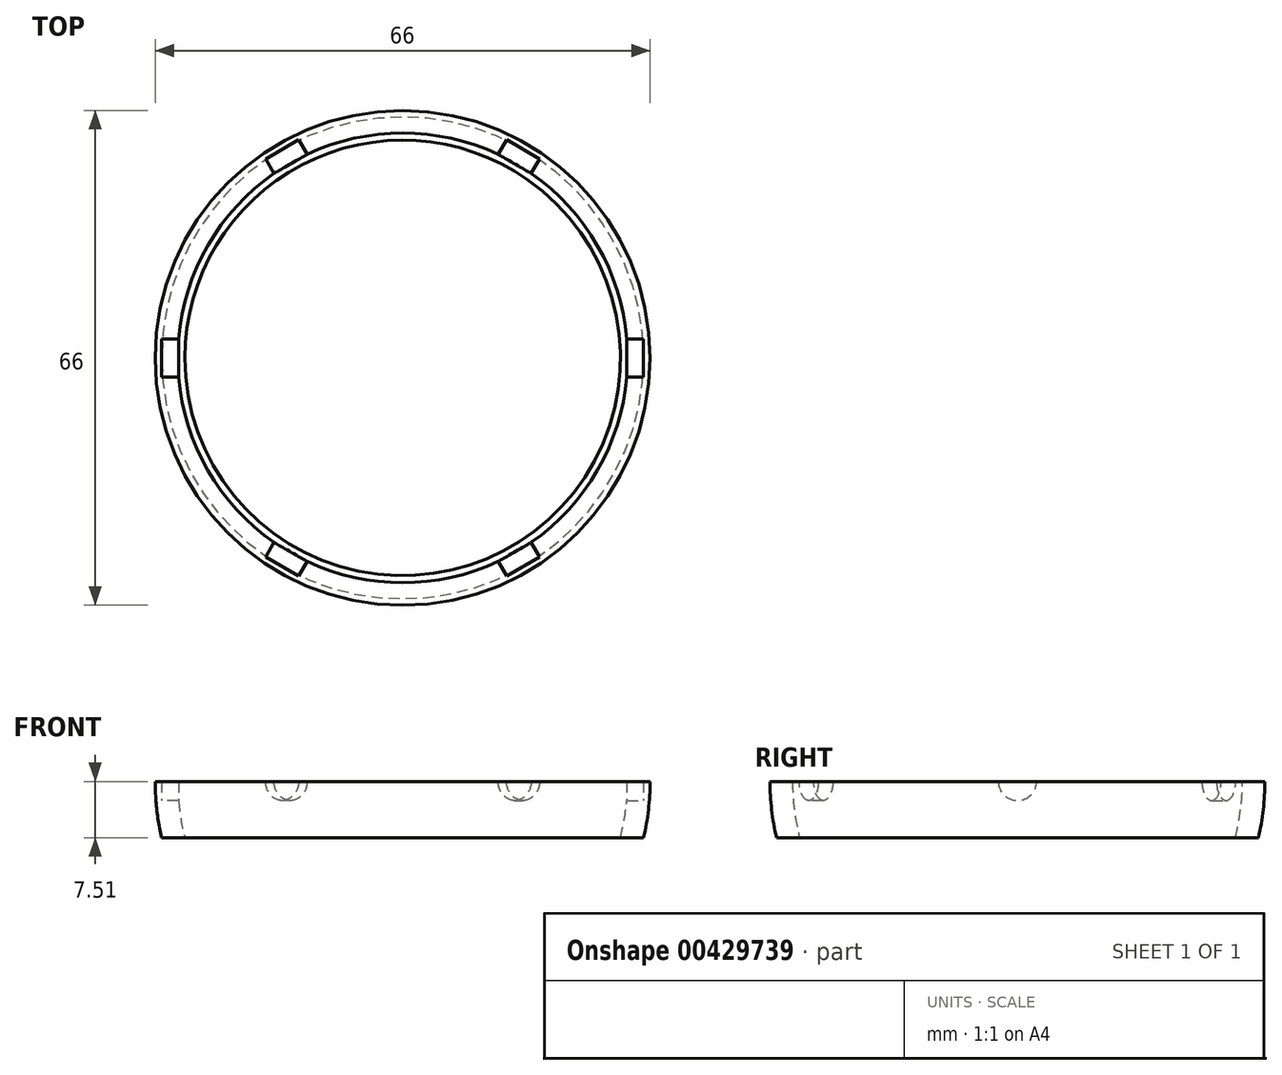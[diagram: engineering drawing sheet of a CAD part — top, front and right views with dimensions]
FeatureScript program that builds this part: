
annotation { "Feature Type Name" : "Feature", "Feature Type Description" : "" }
export const myFeature = defineFeature(function(context is Context, id is Id, definition is map)
    precondition{}
    {
        {
            var Q0;
            Q0=qCreatedBy(makeId("Front.planeOp"),FACE);
            var sketch = newSketch(context, id + "F0", { "sketchPlane" : qUnion([Q0])});
            skLineSegment(sketch, "E0", {"start": v(0, 0) * mm, "end": v(0, 51.6) * mm, "construction": true});
            skArc(sketch, "E1", {"start": v(0, 30) * mm, "mid": v(21.21, 21.21) * mm, "end": v(30, 0) * mm});
            skArc(sketch, "E2", {"start": v(0, 33) * mm, "mid": v(23.33, 23.33) * mm, "end": v(33, 0) * mm});
            skLineSegment(sketch, "E3", {"start": v(30, 0) * mm, "end": v(33, 0) * mm});
            skLineSegment(sketch, "E4", {"start": v(0, 33) * mm, "end": v(0, 30) * mm});
            skLineSegment(sketch, "E5", {"start": v(0, 0) * mm, "end": v(31, 11.29) * mm, "construction": true});
            skLineSegment(sketch, "E6", {"start": v(0, 0) * mm, "end": v(25.28, 21.21) * mm, "construction": true});
            skLineSegment(sketch, "E7", {"start": v(0, 0) * mm, "end": v(16.5, 28.58) * mm, "construction": true});
            skLineSegment(sketch, "E8", {"start": v(5.73, 32.5) * mm, "end": v(0, 0) * mm, "construction": true});
            skLineSegment(sketch, "E9", {"start": v(31, 11.29) * mm, "end": v(35.12, 0) * mm, "construction": true});
            skLineSegment(sketch, "E10", {"start": v(25.28, 21.21) * mm, "end": v(43.08, 0) * mm, "construction": true});
            skLineSegment(sketch, "E11", {"start": v(16.5, 28.58) * mm, "end": v(31, 20.2) * mm, "construction": true});
            skLineSegment(sketch, "E12", {"start": v(5.73, 32.5) * mm, "end": v(16.5, 30.6) * mm, "construction": true});
            skArc(sketch, "E13", {"start": v(30, 0) * mm, "mid": v(29.76, -3.79) * mm, "end": v(29.04, -7.51) * mm});
            skArc(sketch, "E14", {"start": v(33, 0) * mm, "mid": v(32.78, -3.78) * mm, "end": v(32.13, -7.51) * mm});
            skLineSegment(sketch, "E15", {"start": v(32.13, -7.51) * mm, "end": v(29.04, -7.51) * mm});
            skSolve(sketch);
        }
        {
            var Q0;
            Q0=makeQuery(id+"F0.imprint","IMPRINT",FACE,{"disambiguationData":[TD([[makeQuery(id+"F0.imprint","IMPRINT",EDGE,{"derivedFrom":sQuery(id+"F0.wireOp",EDGE,"E1")}),1.0]])]});
            var Q1;
            Q1=makeQuery(id+"F0.imprint","IMPRINT",FACE,{"disambiguationData":[TD([[makeQuery(id+"F0.imprint","IMPRINT",EDGE,{"derivedFrom":sQuery(id+"F0.wireOp",EDGE,"E3")}),-1.0]])]});
            var Q2;
            Q2=sQuery(id+"F0.wireOp",EDGE,"E0");
            revolve(context, id + "F1", {"entities" : qUnion([Q0, Q1]), "axis" : qUnion([Q2]), "revolveType" : RevolveType.SYMMETRIC, "angle" : 60 * degree});
        }
        {
            var Q0;
            Q0=sQuery(id+"F0.wireOp",EDGE,"E9");
            cPlane(context, id + "F2", {"entities" : qUnion([Q0]), "cplaneType" : CPlaneType.LINE_ANGLE, "offset" : 25 * mm, "angle" : 0 * degree, "width" : 150 * mm, "height" : 150 * mm});
        }
        {
            var Q0;
            Q0=sQuery(id+"F0.wireOp",EDGE,"E10");
            cPlane(context, id + "F3", {"entities" : qUnion([Q0]), "cplaneType" : CPlaneType.LINE_ANGLE, "offset" : 25 * mm, "angle" : 0 * degree, "width" : 150 * mm, "height" : 150 * mm});
        }
        {
            var Q0;
            Q0=sQuery(id+"F0.wireOp",EDGE,"E11");
            var Q1;
            Q1=qCreatedBy(makeId("Top.planeOp"),FACE);
            cPlane(context, id + "F4", {"entities" : qUnion([Q0, Q1]), "cplaneType" : CPlaneType.LINE_ANGLE, "offset" : 25 * mm, "angle" : 0 * degree, "width" : 150 * mm, "height" : 150 * mm});
        }
        {
            var Q0;
            Q0=sQuery(id+"F0.wireOp",EDGE,"E12");
            var Q1;
            Q1=qCreatedBy(makeId("Top.planeOp"),FACE);
            cPlane(context, id + "F5", {"entities" : qUnion([Q0, Q1]), "cplaneType" : CPlaneType.LINE_ANGLE, "offset" : 25 * mm, "angle" : 0 * degree, "width" : 150 * mm, "height" : 150 * mm});
        }
        {
            var Q0;
            Q0=qCreatedBy(makeId("Right.planeOp"),FACE);
            var Q1;
            Q1=sQuery(id+"F0.wireOp",VERTEX,"E14.start");
            cPlane(context, id + "F6", {"entities" : qUnion([Q0, Q1]), "cplaneType" : CPlaneType.PLANE_POINT, "offset" : 25 * mm, "width" : 150 * mm, "height" : 150 * mm});
        }
        {
            var Q0;
            Q0=qCreatedBy(id+"F2.planeOp",FACE);
            var sketch = newSketch(context, id + "F7", { "sketchPlane" : qUnion([Q0])});
            skCircle(sketch, "E16", {"center": v(0, 0) * mm, "radius": 2.55 * mm});
            skSolve(sketch);
        }
        {
            var Q0;
            Q0=qCreatedBy(id+"F3.planeOp",FACE);
            var sketch = newSketch(context, id + "F8", { "sketchPlane" : qUnion([Q0])});
            skCircle(sketch, "E17", {"center": v(0, 0) * mm, "radius": 2.55 * mm});
            skSolve(sketch);
        }
        {
            var Q0;
            Q0=qCreatedBy(id+"F4.planeOp",FACE);
            var sketch = newSketch(context, id + "F9", { "sketchPlane" : qUnion([Q0])});
            skCircle(sketch, "E18", {"center": v(0, 0) * mm, "radius": 2.55 * mm});
            skSolve(sketch);
        }
        {
            var Q0;
            Q0=qCreatedBy(id+"F6.planeOp",FACE);
            var sketch = newSketch(context, id + "F10", { "sketchPlane" : qUnion([Q0])});
            skCircle(sketch, "E19", {"center": v(0, 0) * mm, "radius": 2.55 * mm});
            skSolve(sketch);
        }
        {
            var Q0;
            Q0=makeQuery(id+"F7.imprint","IMPRINT",FACE,{"disambiguationData":[TD([[makeQuery(id+"F7.imprint","IMPRINT",EDGE,{"derivedFrom":sQuery(id+"F7.wireOp",EDGE,"E16")}),1.0]])]});
            extrude(context, id + "F11", {"entities" : qUnion([Q0]), "operationType" : NewBodyOperationType.REMOVE, "depth" : 10 * mm});
        }
        {
            var Q0;
            Q0=makeQuery(id+"F8.imprint","IMPRINT",FACE,{"disambiguationData":[TD([[makeQuery(id+"F8.imprint","IMPRINT",EDGE,{"derivedFrom":sQuery(id+"F8.wireOp",EDGE,"E17")}),1.0]])]});
            extrude(context, id + "F12", {"entities" : qUnion([Q0]), "operationType" : NewBodyOperationType.REMOVE, "depth" : 10 * mm});
        }
        {
            var Q0;
            Q0=makeQuery(id+"F9.imprint","IMPRINT",FACE,{"disambiguationData":[TD([[makeQuery(id+"F9.imprint","IMPRINT",EDGE,{"derivedFrom":sQuery(id+"F9.wireOp",EDGE,"E18")}),1.0]])]});
            extrude(context, id + "F13", {"entities" : qUnion([Q0]), "operationType" : NewBodyOperationType.REMOVE, "depth" : 10 * mm});
        }
        {
            var Q0;
            Q0=makeQuery(id+"F10.imprint","IMPRINT",FACE,{"disambiguationData":[TD([[makeQuery(id+"F10.imprint","IMPRINT",EDGE,{"derivedFrom":sQuery(id+"F10.wireOp",EDGE,"E19")}),1.0]])]});
            extrude(context, id + "F14", {"entities" : qUnion([Q0]), "operationType" : NewBodyOperationType.REMOVE, "oppositeDirection" : true, "depth" : 10 * mm});
        }
        {
            var Q0;
            Q0=makeQuery(id+"F1.opRevolve","SWEPT_BODY",BODY,{"disambiguationData":[OSD([sQuery(id+"F0.wireOp",EDGE,"E1"),sQuery(id+"F0.wireOp",EDGE,"E2"),sQuery(id+"F0.wireOp",EDGE,"E3"),sQuery(id+"F0.wireOp",EDGE,"E4")])]});
            var Q1;
            Q1=sQuery(id+"F0.wireOp",EDGE,"E0");
            circularPattern(context, id + "F15", {"operationType" : NewBodyOperationType.ADD, "entities" : qUnion([Q0]), "axis" : qUnion([Q1]), "angle" : 360 * degree, "instanceCount" : 6, "equalSpace" : true});
        }
        {
            var Q0;
            Q0=qCreatedBy(id+"F5.planeOp",FACE);
            var sketch = newSketch(context, id + "F16", { "sketchPlane" : qUnion([Q0])});
            skCircle(sketch, "E20", {"center": v(0, 0) * mm, "radius": 2.55 * mm});
            skSolve(sketch);
        }
        {
            var Q0;
            Q0=makeQuery(id+"F16.imprint","IMPRINT",FACE,{"disambiguationData":[TD([[makeQuery(id+"F16.imprint","IMPRINT",EDGE,{"derivedFrom":sQuery(id+"F16.wireOp",EDGE,"E20")}),1.0]])]});
            extrude(context, id + "F17", {"entities" : qUnion([Q0]), "depth" : 10 * mm});
        }
        {
            var Q0;
            Q0=makeQuery(id+"F17.opExtrude","SWEPT_BODY",BODY,{"disambiguationData":[OSD([sQuery(id+"F16.wireOp",EDGE,"E20")])]});
            var Q1;
            Q1=sQuery(id+"F0.wireOp",EDGE,"E0");
            circularPattern(context, id + "F18", {"operationType" : NewBodyOperationType.REMOVE, "entities" : qUnion([Q0]), "axis" : qUnion([Q1]), "angle" : 360 * degree, "instanceCount" : 6, "equalSpace" : true});
        }
    });
